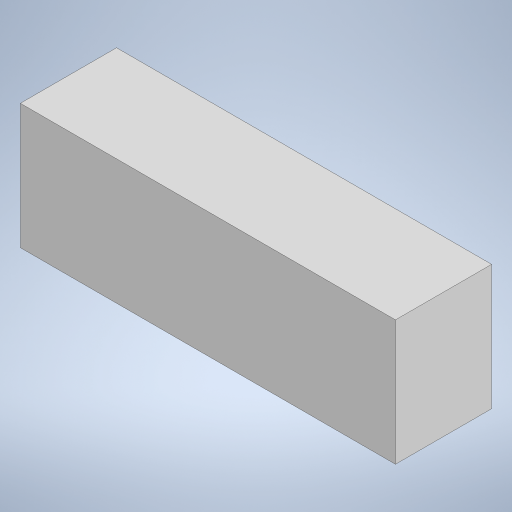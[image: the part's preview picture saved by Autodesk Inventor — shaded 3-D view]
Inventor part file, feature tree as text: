
AUTODESK INVENTOR PART (.ipt)
format: ipt  version: 2023 (Build 270158000, 158)  size: 177,152 bytes
history: native  units: mm
features: other x1, extrude x1, sketch x1
ambient origin geometry x8: Origin, YZ Plane, XZ Plane, XY Plane, X Axis, Y Axis, Z Axis, Center Point
bodies: Body1 (feature_tree)
feature tree (3):
  other  "Těleso1"
  extrude  "Vysunutí1"  Depth=19.5mm
  sketch  "Náčrt1"
